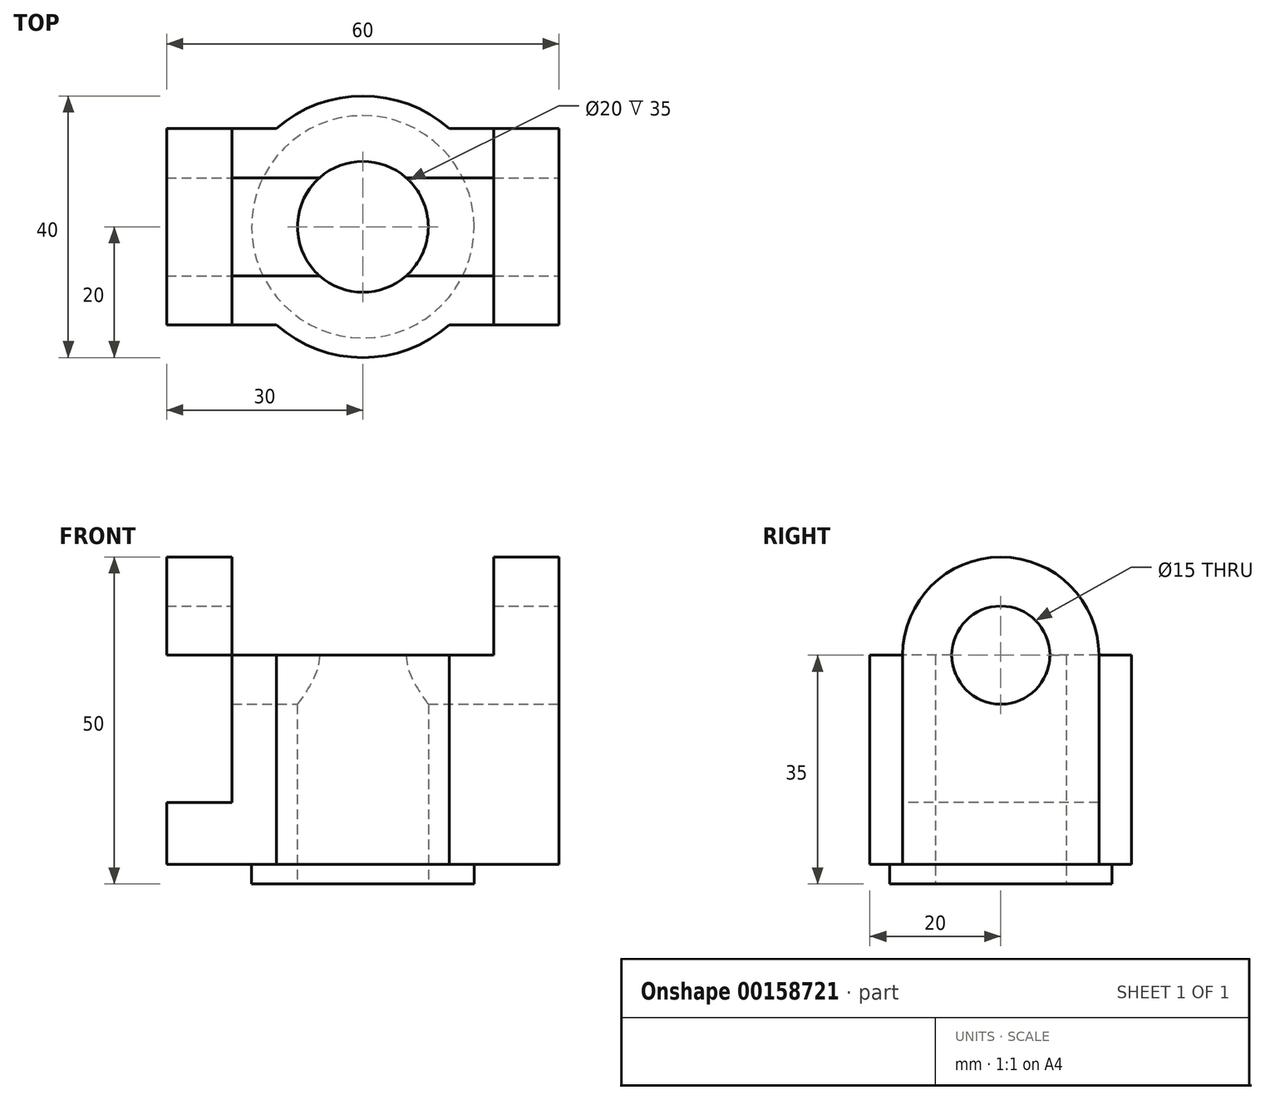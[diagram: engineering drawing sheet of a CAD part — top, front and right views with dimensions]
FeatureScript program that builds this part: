
annotation { "Feature Type Name" : "Feature", "Feature Type Description" : "" }
export const myFeature = defineFeature(function(context is Context, id is Id, definition is map)
    precondition{}
    {
        {
            var Q0;
            Q0=qCreatedBy(makeId("Top.planeOp"),FACE);
            var sketch = newSketch(context, id + "F0", { "sketchPlane" : qUnion([Q0])});
            skCircle(sketch, "E0", {"center": v(0, 0) * mm, "radius": 10 * mm});
            skArc(sketch, "E1", {"start": v(-13.23, -15) * mm, "mid": v(0, -20) * mm, "end": v(13.23, -15) * mm});
            skLineSegment(sketch, "E2.bottom", {"start": v(-30, 15) * mm, "end": v(-13.23, 15) * mm});
            skLineSegment(sketch, "E2.top", {"start": v(-30, -15) * mm, "end": v(-13.23, -15) * mm});
            skLineSegment(sketch, "E2.left", {"start": v(-30, 15) * mm, "end": v(-30, -15) * mm});
            skLineSegment(sketch, "E2.right", {"start": v(30, 15) * mm, "end": v(30, -15) * mm});
            skLineSegment(sketch, "E3", {"start": v(-37.3, 0) * mm, "end": v(47.87, 0) * mm, "construction": true});
            skLineSegment(sketch, "E4", {"start": v(0, 21.01) * mm, "end": v(0, -22.35) * mm, "construction": true});
            skLineSegment(sketch, "E5.trimOffspring", {"start": v(13.23, 15) * mm, "end": v(30, 15) * mm});
            skLineSegment(sketch, "E6.trimOffspring", {"start": v(13.23, -15) * mm, "end": v(30, -15) * mm});
            skArc(sketch, "E7.trimOffspring", {"start": v(13.23, 15) * mm, "mid": v(0, 20) * mm, "end": v(-13.23, 15) * mm});
            skSolve(sketch);
        }
        {
            var Q0;
            Q0=makeQuery(id+"F0.imprint","IMPRINT",FACE,{"disambiguationData":[TD([[makeQuery(id+"F0.imprint","IMPRINT",EDGE,{"derivedFrom":sQuery(id+"F0.wireOp",EDGE,"E0")}),-1.0]])]});
            extrude(context, id + "F1", {"entities" : qUnion([Q0]), "depth" : 32 * mm});
        }
        {
            var Q0;
            Q0=makeQuery(id+"F1.opExtrude","CAP_FACE",FACE,{"disambiguationData":[OSD([sQuery(id+"F0.wireOp",EDGE,"E0"),sQuery(id+"F0.wireOp",EDGE,"E1"),sQuery(id+"F0.wireOp",EDGE,"E2.bottom"),sQuery(id+"F0.wireOp",EDGE,"E2.top"),sQuery(id+"F0.wireOp",EDGE,"E2.left"),sQuery(id+"F0.wireOp",EDGE,"E2.right"),sQuery(id+"F0.wireOp",EDGE,"E5.trimOffspring"),sQuery(id+"F0.wireOp",EDGE,"E6.trimOffspring"),sQuery(id+"F0.wireOp",EDGE,"E7.trimOffspring")])],"isStart":false});
            var sketch = newSketch(context, id + "F2", { "sketchPlane" : qUnion([Q0])});
            skLineSegment(sketch, "E8.0", {"start": v(-30, 15) * mm, "end": v(-30, -15) * mm});
            skLineSegment(sketch, "E9.0", {"start": v(-30, 15) * mm, "end": v(-13.23, 15) * mm});
            skLineSegment(sketch, "E10.0", {"start": v(-30, -15) * mm, "end": v(-13.23, -15) * mm});
            skLineSegment(sketch, "E11.0", {"start": v(13.23, -15) * mm, "end": v(30, -15) * mm});
            skLineSegment(sketch, "E12.0", {"start": v(30, 15) * mm, "end": v(30, -15) * mm});
            skLineSegment(sketch, "E13.0", {"start": v(13.23, 15) * mm, "end": v(30, 15) * mm});
            skLineSegment(sketch, "E14.bottom", {"start": v(-30, 15) * mm, "end": v(-20, 15) * mm});
            skLineSegment(sketch, "E14.top", {"start": v(-30, -15) * mm, "end": v(-20, -15) * mm});
            skLineSegment(sketch, "E14.right", {"start": v(-20, 15) * mm, "end": v(-20, -15) * mm});
            skLineSegment(sketch, "E15.bottom", {"start": v(30, 15) * mm, "end": v(20, 15) * mm});
            skLineSegment(sketch, "E15.top", {"start": v(30, -15) * mm, "end": v(20, -15) * mm});
            skLineSegment(sketch, "E15.right", {"start": v(20, 15) * mm, "end": v(20, -15) * mm});
            skSolve(sketch);
        }
        {
            var Q0;
            Q0=makeQuery(id+"F2.imprint","IMPRINT",FACE,{"disambiguationData":[TD([[makeQuery(id+"F2.imprint","IMPRINT",EDGE,{"derivedFrom":sQuery(id+"F2.wireOp",EDGE,"E9.0")}),-1.0]])]});
            extrude(context, id + "F3", {"entities" : qUnion([Q0]), "operationType" : NewBodyOperationType.REMOVE, "oppositeDirection" : true, "depth" : 22.5 * mm});
        }
        {
            var Q0;
            Q0=makeQuery(id+"F1.opExtrude","CAP_FACE",FACE,{"disambiguationData":[OSD([sQuery(id+"F0.wireOp",EDGE,"E0"),sQuery(id+"F0.wireOp",EDGE,"E1"),sQuery(id+"F0.wireOp",EDGE,"E2.bottom"),sQuery(id+"F0.wireOp",EDGE,"E2.top"),sQuery(id+"F0.wireOp",EDGE,"E2.left"),sQuery(id+"F0.wireOp",EDGE,"E2.right"),sQuery(id+"F0.wireOp",EDGE,"E5.trimOffspring"),sQuery(id+"F0.wireOp",EDGE,"E6.trimOffspring"),sQuery(id+"F0.wireOp",EDGE,"E7.trimOffspring")])],"isStart":true});
            var sketch = newSketch(context, id + "F4", { "sketchPlane" : qUnion([Q0])});
            skCircle(sketch, "E16", {"center": v(0, 0) * mm, "radius": 17 * mm});
            skCircle(sketch, "E17", {"center": v(0, 0) * mm, "radius": 10 * mm});
            skSolve(sketch);
        }
        {
            var Q0;
            Q0=qSketchRegion(id+"F4",true);
            extrude(context, id + "F5", {"entities" : qUnion([Q0]), "operationType" : NewBodyOperationType.ADD, "depth" : 3 * mm});
        }
        {
            var Q0;
            Q0=makeQuery(id+"F1.opExtrude","SWEPT_FACE",FACE,{"disambiguationData":[OSD([sQuery(id+"F0.wireOp",EDGE,"E2.right")])]});
            var sketch = newSketch(context, id + "F6", { "sketchPlane" : qUnion([Q0])});
            skLineSegment(sketch, "E18.0", {"start": v(15, 32) * mm, "end": v(-15, 32) * mm});
            skCircle(sketch, "E19", {"center": v(0, 32) * mm, "radius": 7.5 * mm});
            skArc(sketch, "E20", {"start": v(15, 32) * mm, "mid": v(0, 47) * mm, "end": v(-15, 32) * mm});
            skSolve(sketch);
        }
        {
            var Q0;
            {var subQ0=sQuery(id+"F6.wireOp",EDGE,"E20");Q0=makeQuery(id+"F6.imprint","IMPRINT",FACE,{"disambiguationData":[TD([[makeQuery(id+"F6.imprint","IMPRINT",EDGE,{"derivedFrom":subQ0}),1.0]])]});}
            extrude(context, id + "F7", {"entities" : qUnion([Q0]), "operationType" : NewBodyOperationType.ADD, "oppositeDirection" : true, "depth" : 60 * mm});
        }
        {
            var Q0;
            {var subQ0=sQuery(id+"F6.wireOp",EDGE,"E19");var subQ1=sQuery(id+"F6.wireOp",EDGE,"E18.0");var subQ2=makeQuery(id+"F6.imprint","INTERSECT",VERTEX,{"disambiguationData":[OD(0.0)],"derivedFrom":[subQ1,subQ0]});Q0=makeQuery(id+"F6.imprint","IMPRINT",FACE,{"disambiguationData":[TD([[makeQuery(id+"F6.imprint","IMPRINT",EDGE,{"disambiguationData":[TD([[subQ2,-1.0]])],"derivedFrom":subQ1}),1.0]])]});}
            extrude(context, id + "F8", {"entities" : qUnion([Q0]), "operationType" : NewBodyOperationType.REMOVE, "oppositeDirection" : true, "depth" : 60 * mm});
        }
        {
            var Q0;
            Q0=qCreatedBy(makeId("Front.planeOp"),FACE);
            var sketch = newSketch(context, id + "F9", { "sketchPlane" : qUnion([Q0])});
            skLineSegment(sketch, "E21.0", {"start": v(-20, 32) * mm, "end": v(20, 32) * mm});
            skLineSegment(sketch, "E22.top", {"start": v(-20, 51.35) * mm, "end": v(20, 51.35) * mm});
            skLineSegment(sketch, "E22.left", {"start": v(-20, 32) * mm, "end": v(-20, 51.35) * mm});
            skLineSegment(sketch, "E22.right", {"start": v(20, 32) * mm, "end": v(20, 51.35) * mm});
            skSolve(sketch);
        }
        {
            var Q0;
            Q0=qSketchRegion(id+"F9",true);
            extrude(context, id + "F10", {"entities" : qUnion([Q0]), "operationType" : NewBodyOperationType.REMOVE, "oppositeDirection" : true, "depth" : 25 * mm, "hasSecondDirection" : true, "secondDirectionOppositeDirection" : false, "secondDirectionDepth" : 25 * mm});
        }
    });
